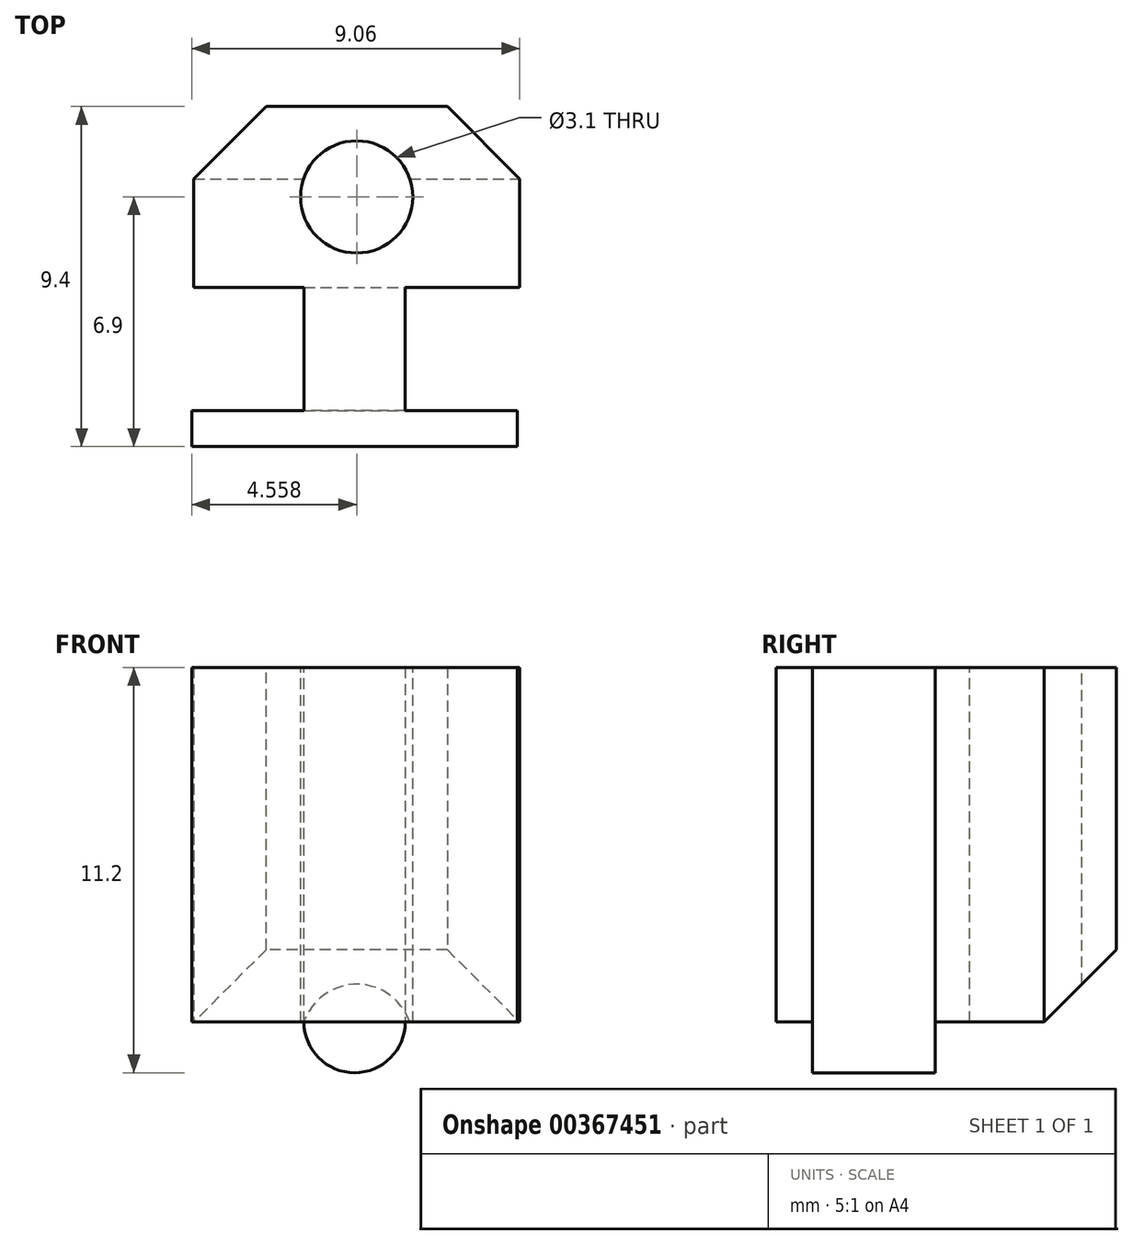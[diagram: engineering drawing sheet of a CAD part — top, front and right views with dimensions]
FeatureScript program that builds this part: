
annotation { "Feature Type Name" : "Feature", "Feature Type Description" : "" }
export const myFeature = defineFeature(function(context is Context, id is Id, definition is map)
    precondition{}
    {
        {
            var Q0;
            Q0=qCreatedBy(makeId("Front.planeOp"),FACE);
            var sketch = newSketch(context, id + "F0", { "sketchPlane" : qUnion([Q0])});
            skLineSegment(sketch, "E0", {"start": v(0, 0) * mm, "end": v(2.8, 0) * mm});
            skLineSegment(sketch, "E1", {"start": v(2.8, 0) * mm, "end": v(2.8, -9.8) * mm});
            skLineSegment(sketch, "E2", {"start": v(0, -9.8) * mm, "end": v(0, 0) * mm});
            skArc(sketch, "E3", {"start": v(0, -9.8) * mm, "mid": v(1.4, -11.2) * mm, "end": v(2.8, -9.8) * mm});
            skSolve(sketch);
        }
        {
            var Q0;
            Q0=qSketchRegion(id+"F0",true);
            extrude(context, id + "F1", {"entities" : qUnion([Q0]), "depth" : 3.4 * mm});
        }
        {
            var Q0;
            Q0=makeQuery(id+"F1.opExtrude","CAP_FACE",FACE,{"disambiguationData":[OSD([sQuery(id+"F0.wireOp",EDGE,"E0"),sQuery(id+"F0.wireOp",EDGE,"E1"),sQuery(id+"F0.wireOp",EDGE,"E2"),sQuery(id+"F0.wireOp",EDGE,"E3")])],"isStart":false});
            var sketch = newSketch(context, id + "F2", { "sketchPlane" : qUnion([Q0])});
            skLineSegment(sketch, "E4", {"start": v(-3.1, 0) * mm, "end": v(5.9, 0) * mm});
            skLineSegment(sketch, "E5", {"start": v(5.9, 0) * mm, "end": v(5.9, -9.8) * mm});
            skLineSegment(sketch, "E6", {"start": v(5.9, -9.8) * mm, "end": v(-3.1, -9.8) * mm});
            skLineSegment(sketch, "E7", {"start": v(-3.1, -9.8) * mm, "end": v(-3.1, 0) * mm});
            skLineSegment(sketch, "E8", {"start": v(1.4, 0) * mm, "end": v(1.4, 0.86) * mm, "construction": true});
            skSolve(sketch);
        }
        {
            var Q0;
            Q0=qSketchRegion(id+"F2",true);
            extrude(context, id + "F3", {"entities" : qUnion([Q0]), "operationType" : NewBodyOperationType.ADD, "depth" : 1 * mm});
        }
        {
            var Q0;
            Q0=makeQuery(id+"F1.opExtrude","CAP_FACE",FACE,{"disambiguationData":[OSD([sQuery(id+"F0.wireOp",EDGE,"E0"),sQuery(id+"F0.wireOp",EDGE,"E1"),sQuery(id+"F0.wireOp",EDGE,"E2"),sQuery(id+"F0.wireOp",EDGE,"E3")])],"isStart":true});
            var sketch = newSketch(context, id + "F4", { "sketchPlane" : qUnion([Q0])});
            skLineSegment(sketch, "E9", {"start": v(-5.96, 0) * mm, "end": v(3.04, 0) * mm});
            skLineSegment(sketch, "E10", {"start": v(3.04, 0) * mm, "end": v(3.04, -9.8) * mm});
            skLineSegment(sketch, "E11", {"start": v(3.04, -9.8) * mm, "end": v(-5.96, -9.8) * mm});
            skLineSegment(sketch, "E12", {"start": v(-5.96, 0) * mm, "end": v(-5.96, -9.8) * mm});
            skSolve(sketch);
        }
        {
            var Q0;
            Q0=qSketchRegion(id+"F4",true);
            extrude(context, id + "F5", {"entities" : qUnion([Q0]), "operationType" : NewBodyOperationType.ADD, "depth" : 5 * mm});
        }
        {
            var Q0;
            Q0=makeQuery(id+"F5.boolean.opBoolean","MERGE",FACE,{"derivedFrom":[makeQuery(id+"F3.boolean.opBoolean","MERGE",FACE,{"derivedFrom":[makeQuery(id+"F1.opExtrude","SWEPT_FACE",FACE,{"disambiguationData":[OSD([sQuery(id+"F0.wireOp",EDGE,"E0")])]}),makeQuery(id+"F3.opExtrude","SWEPT_FACE",FACE,{"disambiguationData":[OSD([sQuery(id+"F2.wireOp",EDGE,"E4")])]})]}),makeQuery(id+"F5.opExtrude","SWEPT_FACE",FACE,{"disambiguationData":[OSD([sQuery(id+"F4.wireOp",EDGE,"E9")])]})]});
            var sketch = newSketch(context, id + "F6", { "sketchPlane" : qUnion([Q0])});
            skPoint(sketch, "E13", {"position": v(1.46, 2.5) * mm});
            skPoint(sketch, "E13.positionSnap0", {"position": v(1.46, 5) * mm});
            skPoint(sketch, "E13.positionSnap1", {"position": v(5.96, 2.5) * mm});
            skSolve(sketch);
        }
        {
            var Q0;
            Q0=sQuery(id+"F6.wireOp",VERTEX,"E13");
            var Q1;
            Q1=makeQuery(id+"F1.opExtrude","SWEPT_BODY",BODY,{"disambiguationData":[OSD([sQuery(id+"F0.wireOp",EDGE,"E0"),sQuery(id+"F0.wireOp",EDGE,"E1"),sQuery(id+"F0.wireOp",EDGE,"E2"),sQuery(id+"F0.wireOp",EDGE,"E3")])]});
            hole(context, id + "F7", {"style" : HoleStyle.SIMPLE, "endStyle" : HoleEndStyle.THROUGH, "holeDiameter" : 3.1 * mm, "startFromSketch" : true, "locations" : qUnion([Q0]), "scope" : qUnion([Q1]), "isTappedThrough" : true});
        }
        {
            var Q0;
            Q0=makeQuery(id+"F5.opExtrude","CAP_EDGE",EDGE,{"disambiguationData":[OSD([sQuery(id+"F4.wireOp",EDGE,"E10")])],"isStart":false});
            var Q1;
            Q1=makeQuery(id+"F5.opExtrude","CAP_EDGE",EDGE,{"disambiguationData":[OSD([sQuery(id+"F4.wireOp",EDGE,"E12")])],"isStart":false});
            var Q2;
            Q2=makeQuery(id+"F5.opExtrude","CAP_EDGE",EDGE,{"disambiguationData":[OSD([sQuery(id+"F4.wireOp",EDGE,"E11")])],"isStart":false});
            chamfer(context, id + "F8", {"entities" : qUnion([Q0, Q1, Q2]), "width" : 2 * mm, "tangentPropagation" : true});
        }
    });
